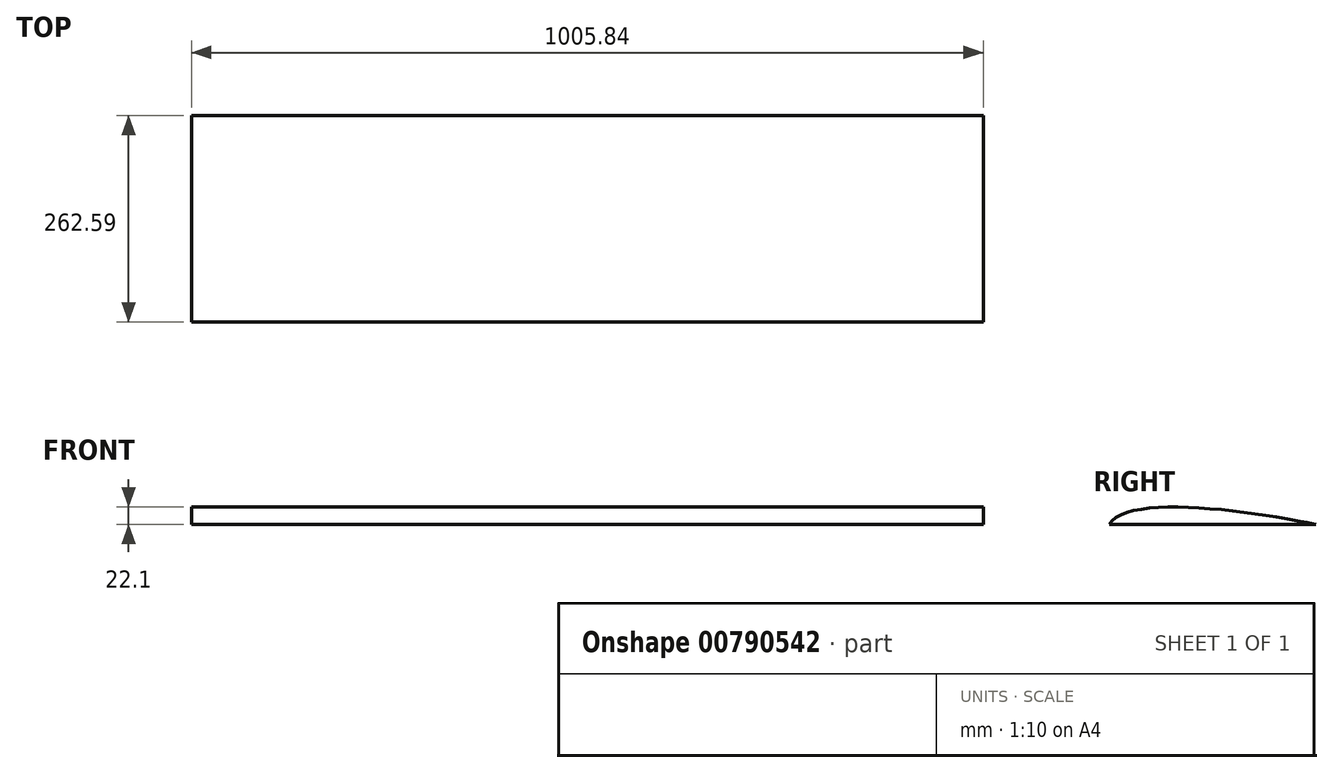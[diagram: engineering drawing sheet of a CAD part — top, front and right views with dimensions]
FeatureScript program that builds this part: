
annotation { "Feature Type Name" : "Feature", "Feature Type Description" : "" }
export const myFeature = defineFeature(function(context is Context, id is Id, definition is map)
    precondition{}
    {
        {
            var Q0;
            Q0=qCreatedBy(makeId("Right.planeOp"),FACE);
            var sketch = newSketch(context, id + "F0", { "sketchPlane" : qUnion([Q0])});
            skLineSegment(sketch, "E0", {"start": v(-130.4, 0) * mm, "end": v(132.2, 0) * mm});
            skFitSpline(sketch, "E1", {"points": [v(-130.4, 0) * mm, v(132.2, 0) * mm], "startDerivative": vector(64.97, 116.86) * mm, "endDerivative": vector(257.18, -54.6) * mm});
            skSolve(sketch);
        }
        {
            var Q0;
            Q0 = qSketchRegion(id + "F0", true);
            extrude(context, id + "F1", {"entities" : qUnion([Q0]), "endBound" : BoundingType.SYMMETRIC, "depth" : 1005.84 * mm, "offsetDistance" : 25.4 * mm});
        }
    });
